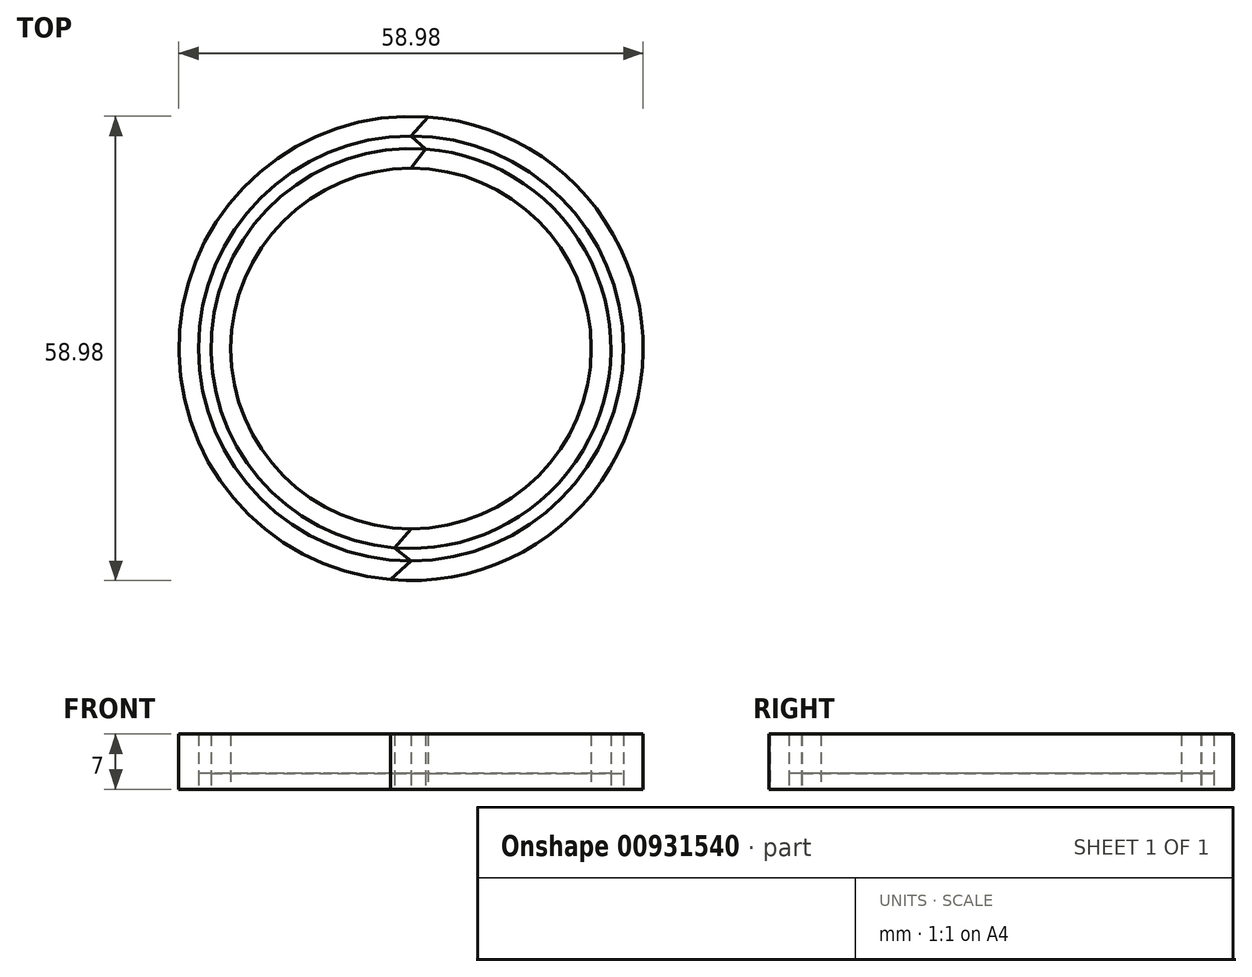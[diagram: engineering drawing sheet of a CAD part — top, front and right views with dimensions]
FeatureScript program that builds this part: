
annotation { "Feature Type Name" : "Feature", "Feature Type Description" : "" }
export const myFeature = defineFeature(function(context is Context, id is Id, definition is map)
    precondition{}
    {
        {
            var Q0;
            Q0=qCreatedBy(makeId("Top.planeOp"),FACE);
            var sketch = newSketch(context, id + "F0", { "sketchPlane" : qUnion([Q0])});
            skCircle(sketch, "E0", {"center": v(0, 0) * mm, "radius": 25.4 * mm});
            skCircle(sketch, "E1", {"center": v(0, 0) * mm, "radius": 26.99 * mm});
            skCircle(sketch, "E2", {"center": v(0, 0) * mm, "radius": 29.49 * mm});
            skCircle(sketch, "E3", {"center": v(0, 0) * mm, "radius": 22.9 * mm});
            skLineSegment(sketch, "E4", {"start": v(0, 22.9) * mm, "end": v(1.88, 25.33) * mm});
            skLineSegment(sketch, "E5", {"start": v(1.88, 25.33) * mm, "end": v(0, 26.99) * mm});
            skLineSegment(sketch, "E6", {"start": v(0, 26.99) * mm, "end": v(2.14, 29.4) * mm});
            skLineSegment(sketch, "E7", {"start": v(0, -22.9) * mm, "end": v(-2.1, -25.31) * mm});
            skLineSegment(sketch, "E8", {"start": v(-2.1, -25.31) * mm, "end": v(0, -26.99) * mm});
            skLineSegment(sketch, "E9", {"start": v(0, -26.99) * mm, "end": v(-2.6, -29.37) * mm});
            skSolve(sketch);
        }
        {
            var Q0;
            {var subQ0=sQuery(id+"F0.wireOp",EDGE,"E4");Q0=makeQuery(id+"F0.imprint","IMPRINT",FACE,{"disambiguationData":[TD([[makeQuery(id+"F0.imprint","IMPRINT",EDGE,{"derivedFrom":subQ0}),-1.0]])]});}
            var Q1;
            {var subQ0=sQuery(id+"F0.wireOp",EDGE,"E6");Q1=makeQuery(id+"F0.imprint","IMPRINT",FACE,{"disambiguationData":[TD([[makeQuery(id+"F0.imprint","IMPRINT",EDGE,{"derivedFrom":subQ0}),-1.0]])]});}
            extrude(context, id + "F1", {"entities" : qUnion([Q0, Q1]), "depth" : 7 * mm, "offsetDistance" : 25 * mm});
        }
        {
            var Q0;
            {var subQ0=sQuery(id+"F0.wireOp",EDGE,"E6");Q0=makeQuery(id+"F0.imprint","IMPRINT",FACE,{"disambiguationData":[TD([[makeQuery(id+"F0.imprint","IMPRINT",EDGE,{"derivedFrom":subQ0}),1.0]])]});}
            var Q1;
            {var subQ0=sQuery(id+"F0.wireOp",EDGE,"E4");Q1=makeQuery(id+"F0.imprint","IMPRINT",FACE,{"disambiguationData":[TD([[makeQuery(id+"F0.imprint","IMPRINT",EDGE,{"derivedFrom":subQ0}),1.0]])]});}
            extrude(context, id + "F2", {"entities" : qUnion([Q0, Q1]), "depth" : 7 * mm, "offsetDistance" : 25 * mm});
        }
        {
            var Q0;
            {var subQ0=sQuery(id+"F0.wireOp",EDGE,"E5");Q0=makeQuery(id+"F0.imprint","IMPRINT",FACE,{"disambiguationData":[TD([[makeQuery(id+"F0.imprint","IMPRINT",EDGE,{"derivedFrom":subQ0}),-1.0]])]});}
            extrude(context, id + "F3", {"entities" : qUnion([Q0]), "depth" : 2 * mm, "offsetDistance" : 25 * mm});
        }
        {
            var Q0;
            {var subQ0=sQuery(id+"F0.wireOp",EDGE,"E5");Q0=makeQuery(id+"F0.imprint","IMPRINT",FACE,{"disambiguationData":[TD([[makeQuery(id+"F0.imprint","IMPRINT",EDGE,{"derivedFrom":subQ0}),1.0]])]});}
            extrude(context, id + "F4", {"entities" : qUnion([Q0]), "depth" : 2 * mm, "offsetDistance" : 25 * mm});
        }
    });
